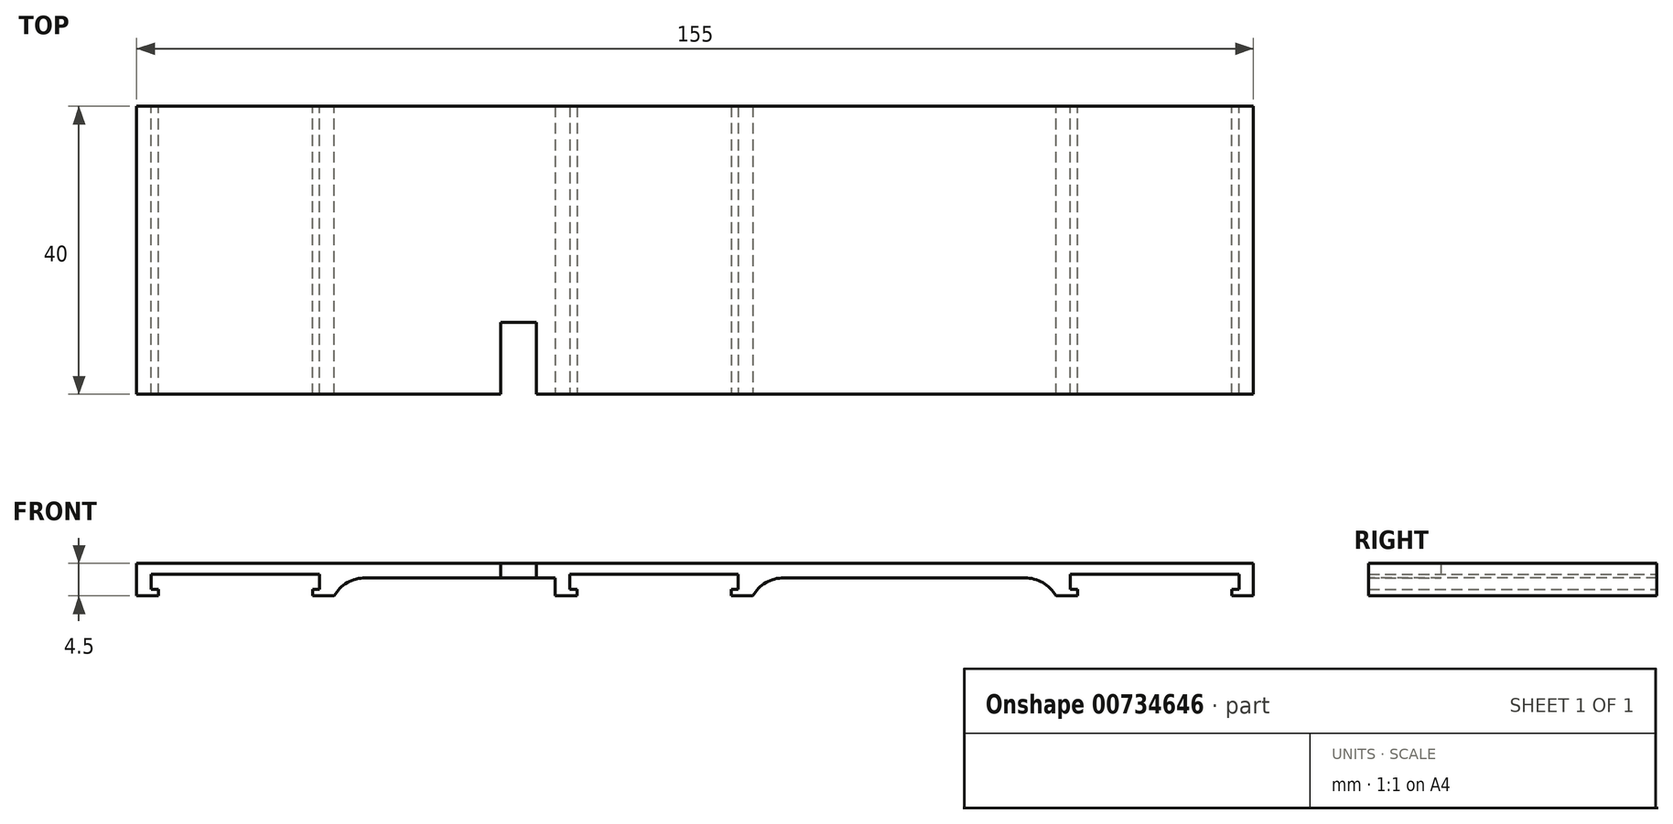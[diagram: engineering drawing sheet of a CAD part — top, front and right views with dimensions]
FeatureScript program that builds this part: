
annotation { "Feature Type Name" : "Feature", "Feature Type Description" : "" }
export const myFeature = defineFeature(function(context is Context, id is Id, definition is map)
    precondition{}
    {
        {
            var Q0;
            Q0=qCreatedBy(makeId("Front.planeOp"),FACE);
            var sketch = newSketch(context, id + "F0", { "sketchPlane" : qUnion([Q0])});
            skLineSegment(sketch, "E0.bottom", {"start": v(0, 0) * mm, "end": v(77.5, 0) * mm});
            skLineSegment(sketch, "E0.top", {"start": v(0, -2) * mm, "end": v(50.1, -2) * mm});
            skLineSegment(sketch, "E0.left", {"start": v(0, 0) * mm, "end": v(0, -2) * mm});
            skLineSegment(sketch, "E0.right", {"start": v(77.5, 0) * mm, "end": v(77.5, -2) * mm});
            skLineSegment(sketch, "E1.top", {"start": v(77.5, -4.5) * mm, "end": v(74.5, -4.5) * mm});
            skLineSegment(sketch, "E1.left", {"start": v(77.5, -2) * mm, "end": v(77.5, -4.5) * mm});
            skLineSegment(sketch, "E1.right", {"start": v(74.5, -3.6) * mm, "end": v(74.5, -4.5) * mm});
            skLineSegment(sketch, "E2", {"start": v(74.5, -3.6) * mm, "end": v(75.5, -3.6) * mm});
            skLineSegment(sketch, "E3", {"start": v(75.5, -3.6) * mm, "end": v(75.5, -2) * mm});
            skLineSegment(sketch, "E4.top", {"start": v(50.1, -4.5) * mm, "end": v(53.1, -4.5) * mm});
            skLineSegment(sketch, "E4.left", {"start": v(50.1, -2) * mm, "end": v(50.1, -4.5) * mm});
            skLineSegment(sketch, "E4.right", {"start": v(53.1, -3.6) * mm, "end": v(53.1, -4.5) * mm});
            skLineSegment(sketch, "E5", {"start": v(53.1, -3.6) * mm, "end": v(52.1, -3.6) * mm});
            skLineSegment(sketch, "E6", {"start": v(52.1, -3.6) * mm, "end": v(52.1, -2) * mm});
            skLineSegment(sketch, "E7", {"start": v(52.1, -2) * mm, "end": v(52.1, -1.5) * mm});
            skLineSegment(sketch, "E8", {"start": v(52.1, -1.5) * mm, "end": v(75.5, -1.5) * mm});
            skLineSegment(sketch, "E9", {"start": v(75.5, -1.5) * mm, "end": v(75.5, -2) * mm});
            skSolve(sketch);
        }
        {
            var Q0;
            Q0 = qSketchRegion(id + "F0", true);
            extrude(context, id + "F1", {"entities" : qUnion([Q0]), "depth" : 40 * mm, "offsetDistance" : 25 * mm});
        }
        {
            var Q0;
            Q0=makeQuery(id+"F1.opExtrude","SWEPT_EDGE",EDGE,{"disambiguationData":[OSD([sQuery(id+"F0.wireOp",EDGE,"E0.top"),sQuery(id+"F0.wireOp",EDGE,"E4.left")])]});
            fillet(context, id + "F2", {"entities" : qUnion([Q0]), "tangentPropagation" : true, "radius" : 5 * mm, "defaultsChanged" : false, "vertexSettings" : [], "allowEdgeOverflow" : false});
        }
        {
            var Q0;
            Q0=makeQuery(id+"F1.opExtrude","SWEPT_BODY",BODY,{"disambiguationData":[OSD([sQuery(id+"F0.wireOp",EDGE,"E0.bottom"),sQuery(id+"F0.wireOp",EDGE,"E0.top"),sQuery(id+"F0.wireOp",EDGE,"E0.left"),sQuery(id+"F0.wireOp",EDGE,"E0.right"),sQuery(id+"F0.wireOp",EDGE,"E1.bottom"),sQuery(id+"F0.wireOp",EDGE,"E1.top"),sQuery(id+"F0.wireOp",EDGE,"E1.left"),sQuery(id+"F0.wireOp",EDGE,"E1.right"),sQuery(id+"F0.wireOp",EDGE,"E2"),sQuery(id+"F0.wireOp",EDGE,"E3"),sQuery(id+"F0.wireOp",EDGE,"E4.bottom"),sQuery(id+"F0.wireOp",EDGE,"E4.top"),sQuery(id+"F0.wireOp",EDGE,"E4.left"),sQuery(id+"F0.wireOp",EDGE,"E4.right"),sQuery(id+"F0.wireOp",EDGE,"E5"),sQuery(id+"F0.wireOp",EDGE,"E6"),sQuery(id+"F0.wireOp",EDGE,"048939d6-e767-44c0-839d-1c3795db7b53.trimOffspring")])]});
            var Q1;
            Q1=qCreatedBy(makeId("Right.planeOp"),FACE);
            mirror(context, id + "F3", {"operationType" : NewBodyOperationType.ADD, "entities" : qUnion([Q0]), "mirrorPlane" : qUnion([Q1])});
        }
        {
            var Q0;
            {var subQ0=makeQuery(id+"F1.opExtrude","CAP_FACE",FACE,{"disambiguationData":[OSD([sQuery(id+"F0.wireOp",EDGE,"E0.bottom"),sQuery(id+"F0.wireOp",EDGE,"E0.top"),sQuery(id+"F0.wireOp",EDGE,"E0.left"),sQuery(id+"F0.wireOp",EDGE,"E0.right"),sQuery(id+"F0.wireOp",EDGE,"E1.bottom"),sQuery(id+"F0.wireOp",EDGE,"E1.top"),sQuery(id+"F0.wireOp",EDGE,"E1.left"),sQuery(id+"F0.wireOp",EDGE,"E1.right"),sQuery(id+"F0.wireOp",EDGE,"E2"),sQuery(id+"F0.wireOp",EDGE,"E3"),sQuery(id+"F0.wireOp",EDGE,"E4.bottom"),sQuery(id+"F0.wireOp",EDGE,"E4.top"),sQuery(id+"F0.wireOp",EDGE,"E4.left"),sQuery(id+"F0.wireOp",EDGE,"E4.right"),sQuery(id+"F0.wireOp",EDGE,"E5"),sQuery(id+"F0.wireOp",EDGE,"E6"),sQuery(id+"F0.wireOp",EDGE,"048939d6-e767-44c0-839d-1c3795db7b53.trimOffspring")])],"isStart":false});Q0=makeQuery(id+"F3.boolean.opBoolean","MERGE",FACE,{"derivedFrom":[subQ0,makeQuery(id+"F3.opPattern","COPY",FACE,{"derivedFrom":subQ0,"instanceName":"1"})]});}
            var sketch = newSketch(context, id + "F4", { "sketchPlane" : qUnion([Q0])});
            skLineSegment(sketch, "E10.top", {"start": v(-17.4, -3.6) * mm, "end": v(6, -3.6) * mm, "construction": true});
            skLineSegment(sketch, "E10.left", {"start": v(-17.4, -2) * mm, "end": v(-17.4, -3.6) * mm, "construction": true});
            skLineSegment(sketch, "E10.right", {"start": v(6, -2) * mm, "end": v(6, -3.6) * mm, "construction": true});
            skLineSegment(sketch, "E11.bottom", {"start": v(-17.4, -2) * mm, "end": v(-19.4, -2) * mm});
            skLineSegment(sketch, "E11.top", {"start": v(-17.4, -4.5) * mm, "end": v(-19.4, -4.5) * mm});
            skLineSegment(sketch, "E11.left", {"start": v(-17.4, -2) * mm, "end": v(-17.4, -3.6) * mm});
            skLineSegment(sketch, "E11.right", {"start": v(-19.4, -2) * mm, "end": v(-19.4, -4.5) * mm});
            skLineSegment(sketch, "E12.bottom", {"start": v(-17.4, -3.6) * mm, "end": v(-16.4, -3.6) * mm});
            skLineSegment(sketch, "E12.top", {"start": v(-17.4, -4.5) * mm, "end": v(-16.4, -4.5) * mm});
            skLineSegment(sketch, "E12.right", {"start": v(-16.4, -3.6) * mm, "end": v(-16.4, -4.5) * mm});
            skLineSegment(sketch, "E13.bottom", {"start": v(6, -2) * mm, "end": v(8, -2) * mm});
            skLineSegment(sketch, "E13.top", {"start": v(6, -4.5) * mm, "end": v(8, -4.5) * mm});
            skLineSegment(sketch, "E13.left", {"start": v(6, -2) * mm, "end": v(6, -3.6) * mm});
            skLineSegment(sketch, "E13.right", {"start": v(8, -2) * mm, "end": v(8, -4.5) * mm});
            skLineSegment(sketch, "E14.bottom", {"start": v(6, -3.6) * mm, "end": v(5, -3.6) * mm});
            skLineSegment(sketch, "E14.top", {"start": v(6, -4.5) * mm, "end": v(5, -4.5) * mm});
            skLineSegment(sketch, "E14.right", {"start": v(5, -3.6) * mm, "end": v(5, -4.5) * mm});
            skLineSegment(sketch, "E15", {"start": v(6, -2) * mm, "end": v(6, -1.5) * mm});
            skLineSegment(sketch, "E16", {"start": v(6, -1.5) * mm, "end": v(-17.4, -1.5) * mm});
            skLineSegment(sketch, "E17", {"start": v(-17.4, -1.5) * mm, "end": v(-17.4, -2) * mm});
            skSolve(sketch);
        }
        {
            var Q0;
            Q0 = qSketchRegion(id + "F4", true);
            var Q1;
            {var subQ0=makeQuery(id+"F1.opExtrude","CAP_FACE",FACE,{"disambiguationData":[OSD([sQuery(id+"F0.wireOp",EDGE,"E0.bottom"),sQuery(id+"F0.wireOp",EDGE,"E0.top"),sQuery(id+"F0.wireOp",EDGE,"E0.left"),sQuery(id+"F0.wireOp",EDGE,"E0.right"),sQuery(id+"F0.wireOp",EDGE,"E1.bottom"),sQuery(id+"F0.wireOp",EDGE,"E1.top"),sQuery(id+"F0.wireOp",EDGE,"E1.left"),sQuery(id+"F0.wireOp",EDGE,"E1.right"),sQuery(id+"F0.wireOp",EDGE,"E2"),sQuery(id+"F0.wireOp",EDGE,"E3"),sQuery(id+"F0.wireOp",EDGE,"E4.bottom"),sQuery(id+"F0.wireOp",EDGE,"E4.top"),sQuery(id+"F0.wireOp",EDGE,"E4.left"),sQuery(id+"F0.wireOp",EDGE,"E4.right"),sQuery(id+"F0.wireOp",EDGE,"E5"),sQuery(id+"F0.wireOp",EDGE,"E6"),sQuery(id+"F0.wireOp",EDGE,"048939d6-e767-44c0-839d-1c3795db7b53.trimOffspring")])],"isStart":true});Q1=makeQuery(id+"F3.boolean.opBoolean","MERGE",FACE,{"derivedFrom":[subQ0,makeQuery(id+"F3.opPattern","COPY",FACE,{"derivedFrom":subQ0,"instanceName":"1"})]});}
            extrude(context, id + "F5", {"entities" : qUnion([Q0]), "operationType" : NewBodyOperationType.ADD, "endBound" : BoundingType.UP_TO_SURFACE, "oppositeDirection" : true, "depth" : 40 * mm, "endBoundEntityFace" : qUnion([Q1]), "offsetDistance" : 25 * mm});
        }
        {
            var Q0;
            {var subQ0=makeQuery(id+"F1.opExtrude","CAP_FACE",FACE,{"disambiguationData":[OSD([sQuery(id+"F0.wireOp",EDGE,"E0.bottom"),sQuery(id+"F0.wireOp",EDGE,"E0.top"),sQuery(id+"F0.wireOp",EDGE,"E0.left"),sQuery(id+"F0.wireOp",EDGE,"E0.right"),sQuery(id+"F0.wireOp",EDGE,"E1.top"),sQuery(id+"F0.wireOp",EDGE,"E1.left"),sQuery(id+"F0.wireOp",EDGE,"E1.right"),sQuery(id+"F0.wireOp",EDGE,"E2"),sQuery(id+"F0.wireOp",EDGE,"E3"),sQuery(id+"F0.wireOp",EDGE,"E4.top"),sQuery(id+"F0.wireOp",EDGE,"E4.left"),sQuery(id+"F0.wireOp",EDGE,"E4.right"),sQuery(id+"F0.wireOp",EDGE,"E5"),sQuery(id+"F0.wireOp",EDGE,"E6"),sQuery(id+"F0.wireOp",EDGE,"E7"),sQuery(id+"F0.wireOp",EDGE,"E8"),sQuery(id+"F0.wireOp",EDGE,"E9")])],"isStart":true});Q0=makeQuery(id+"F5.boolean.opBoolean","MERGE",FACE,{"derivedFrom":[makeQuery(id+"F3.boolean.opBoolean","MERGE",FACE,{"derivedFrom":[subQ0,makeQuery(id+"F3.opPattern","COPY",FACE,{"derivedFrom":subQ0,"instanceName":"1"})]}),makeQuery(id+"F5.opExtrude","CAP_FACE",FACE,{"disambiguationData":[OSD([sQuery(id+"F4.wireOp",EDGE,"E11.bottom"),sQuery(id+"F4.wireOp",EDGE,"E11.top"),sQuery(id+"F4.wireOp",EDGE,"E11.left"),sQuery(id+"F4.wireOp",EDGE,"E11.right"),sQuery(id+"F4.wireOp",EDGE,"E12.bottom"),sQuery(id+"F4.wireOp",EDGE,"E12.top"),sQuery(id+"F4.wireOp",EDGE,"E12.right")])],"isStart":false}),makeQuery(id+"F5.opExtrude","CAP_FACE",FACE,{"disambiguationData":[OSD([sQuery(id+"F4.wireOp",EDGE,"E13.bottom"),sQuery(id+"F4.wireOp",EDGE,"E13.top"),sQuery(id+"F4.wireOp",EDGE,"E13.left"),sQuery(id+"F4.wireOp",EDGE,"E13.right"),sQuery(id+"F4.wireOp",EDGE,"E14.bottom"),sQuery(id+"F4.wireOp",EDGE,"E14.top"),sQuery(id+"F4.wireOp",EDGE,"E14.right")])],"isStart":false})]});}
            var sketch = newSketch(context, id + "F6", { "sketchPlane" : qUnion([Q0])});
            skLineSegment(sketch, "E18.bottom", {"start": v(-6, -2) * mm, "end": v(17.4, -2) * mm});
            skLineSegment(sketch, "E18.top", {"start": v(-6, -1.5) * mm, "end": v(17.4, -1.5) * mm});
            skLineSegment(sketch, "E18.left", {"start": v(-6, -2) * mm, "end": v(-6, -1.5) * mm});
            skLineSegment(sketch, "E18.right", {"start": v(17.4, -2) * mm, "end": v(17.4, -1.5) * mm});
            skSolve(sketch);
        }
        {
            var Q0;
            Q0 = qSketchRegion(id + "F6", true);
            extrude(context, id + "F7", {"entities" : qUnion([Q0]), "operationType" : NewBodyOperationType.REMOVE, "endBound" : BoundingType.THROUGH_ALL, "oppositeDirection" : true, "depth" : 25 * mm, "offsetDistance" : 25 * mm});
        }
        {
            var Q0;
            Q0=makeQuery(id+"F5.opExtrude","SWEPT_EDGE",EDGE,{"disambiguationData":[OSD([sQuery(id+"F0.wireOp",EDGE,"E0.top"),sQuery(id+"F4.wireOp",EDGE,"E11.bottom"),sQuery(id+"F4.wireOp",EDGE,"E11.right")])]});
            var Q1;
            Q1=makeQuery(id+"F5.opExtrude","SWEPT_EDGE",EDGE,{"disambiguationData":[OSD([sQuery(id+"F0.wireOp",EDGE,"E0.top"),sQuery(id+"F4.wireOp",EDGE,"E13.bottom"),sQuery(id+"F4.wireOp",EDGE,"E13.right")])]});
            fillet(context, id + "F8", {"entities" : qUnion([Q0, Q1]), "tangentPropagation" : true, "radius" : 5 * mm, "defaultsChanged" : false, "vertexSettings" : [], "allowEdgeOverflow" : false});
        }
        {
            var Q0;
            Q0=qCreatedBy(makeId("Top.planeOp"),FACE);
            var sketch = newSketch(context, id + "F9", { "sketchPlane" : qUnion([Q0])});
            skLineSegment(sketch, "E19.bottom", {"start": v(-27, -40) * mm, "end": v(-22, -40) * mm});
            skLineSegment(sketch, "E19.top", {"start": v(-27, -30) * mm, "end": v(-22, -30) * mm});
            skLineSegment(sketch, "E19.left", {"start": v(-27, -30) * mm, "end": v(-27, -40) * mm});
            skLineSegment(sketch, "E19.right", {"start": v(-22, -30) * mm, "end": v(-22, -40) * mm});
            skSolve(sketch);
        }
        {
            var Q0;
            Q0 = qSketchRegion(id + "F9", true);
            extrude(context, id + "F10", {"entities" : qUnion([Q0]), "operationType" : NewBodyOperationType.REMOVE, "endBound" : BoundingType.THROUGH_ALL, "depth" : 25 * mm, "offsetDistance" : 25 * mm, "hasSecondDirection" : true, "secondDirectionBound" : SecondDirectionBoundingType.THROUGH_ALL, "secondDirectionOppositeDirection" : true, "secondDirectionDepth" : 25 * mm});
        }
    });
